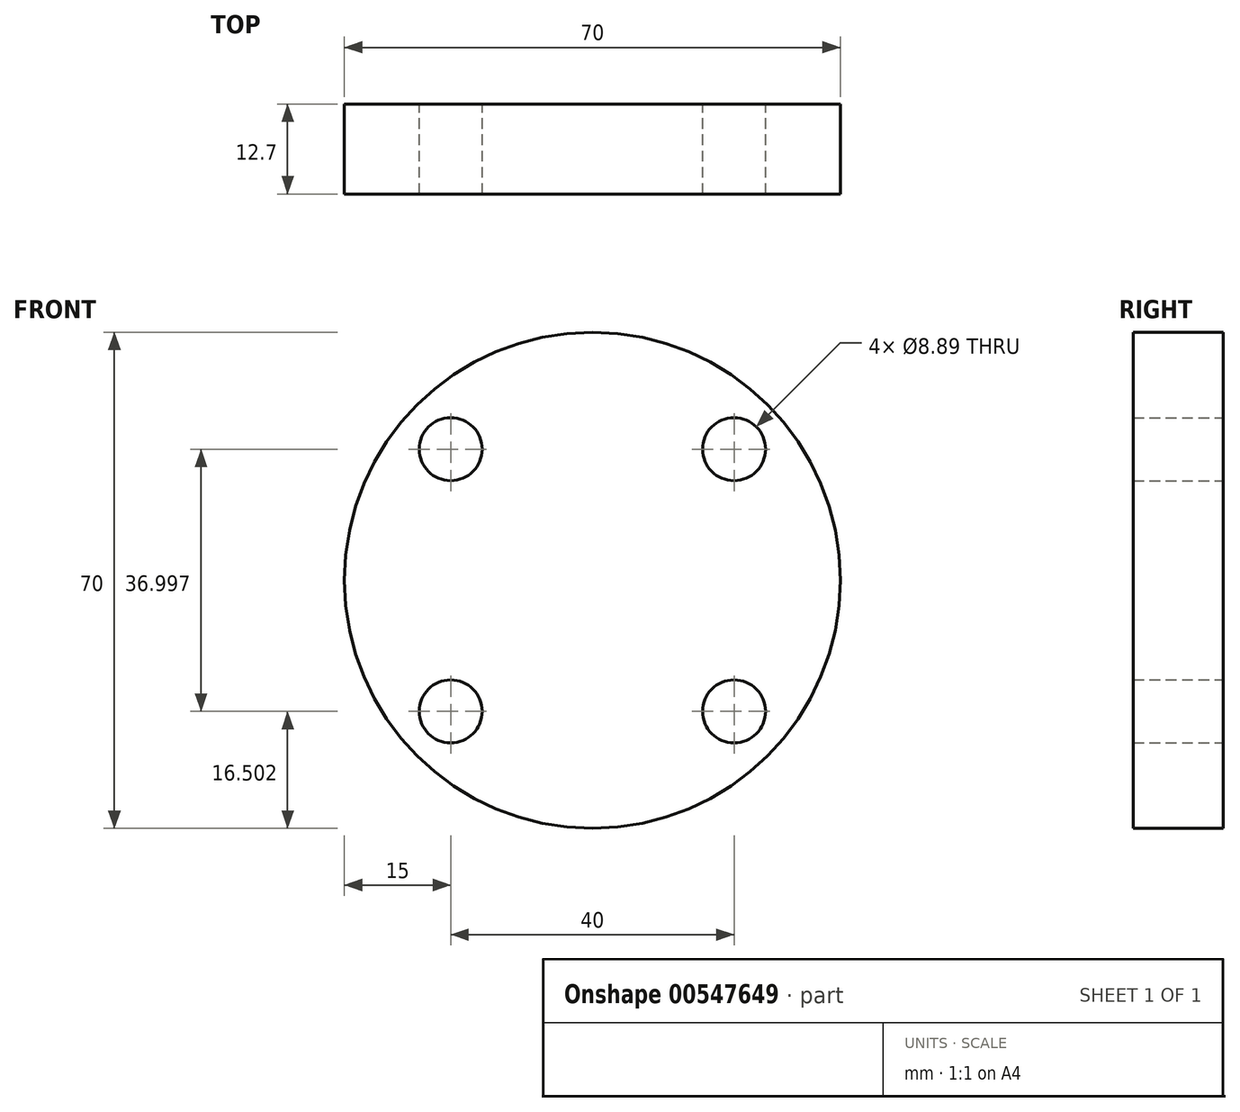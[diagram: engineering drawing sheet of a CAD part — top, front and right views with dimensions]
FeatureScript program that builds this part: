
annotation { "Feature Type Name" : "Feature", "Feature Type Description" : "" }
export const myFeature = defineFeature(function(context is Context, id is Id, definition is map)
    precondition{}
    {
        {
            var Q0;
            Q0=qCreatedBy(makeId("Front.planeOp"),FACE);
            var sketch = newSketch(context, id + "F0", { "sketchPlane" : qUnion([Q0])});
            skCircle(sketch, "E0", {"center": v(0, 0) * mm, "radius": 35 * mm});
            skCircle(sketch, "E1", {"center": v(-20, 18.5) * mm, "radius": 4.45 * mm});
            skCircle(sketch, "E2.MirrorC", {"center": v(20, 18.5) * mm, "radius": 4.45 * mm});
            skCircle(sketch, "E3.MirrorC", {"center": v(-20, -18.5) * mm, "radius": 4.45 * mm});
            skCircle(sketch, "E4.MirrorC", {"center": v(20, -18.5) * mm, "radius": 4.45 * mm});
            skSolve(sketch);
        }
        {
            var Q0;
            Q0 = qSketchRegion(id + "F0", true);
            extrude(context, id + "F1", {"entities" : qUnion([Q0]), "depth" : 12.7 * mm, "offsetDistance" : 25.4 * mm});
        }
    });
